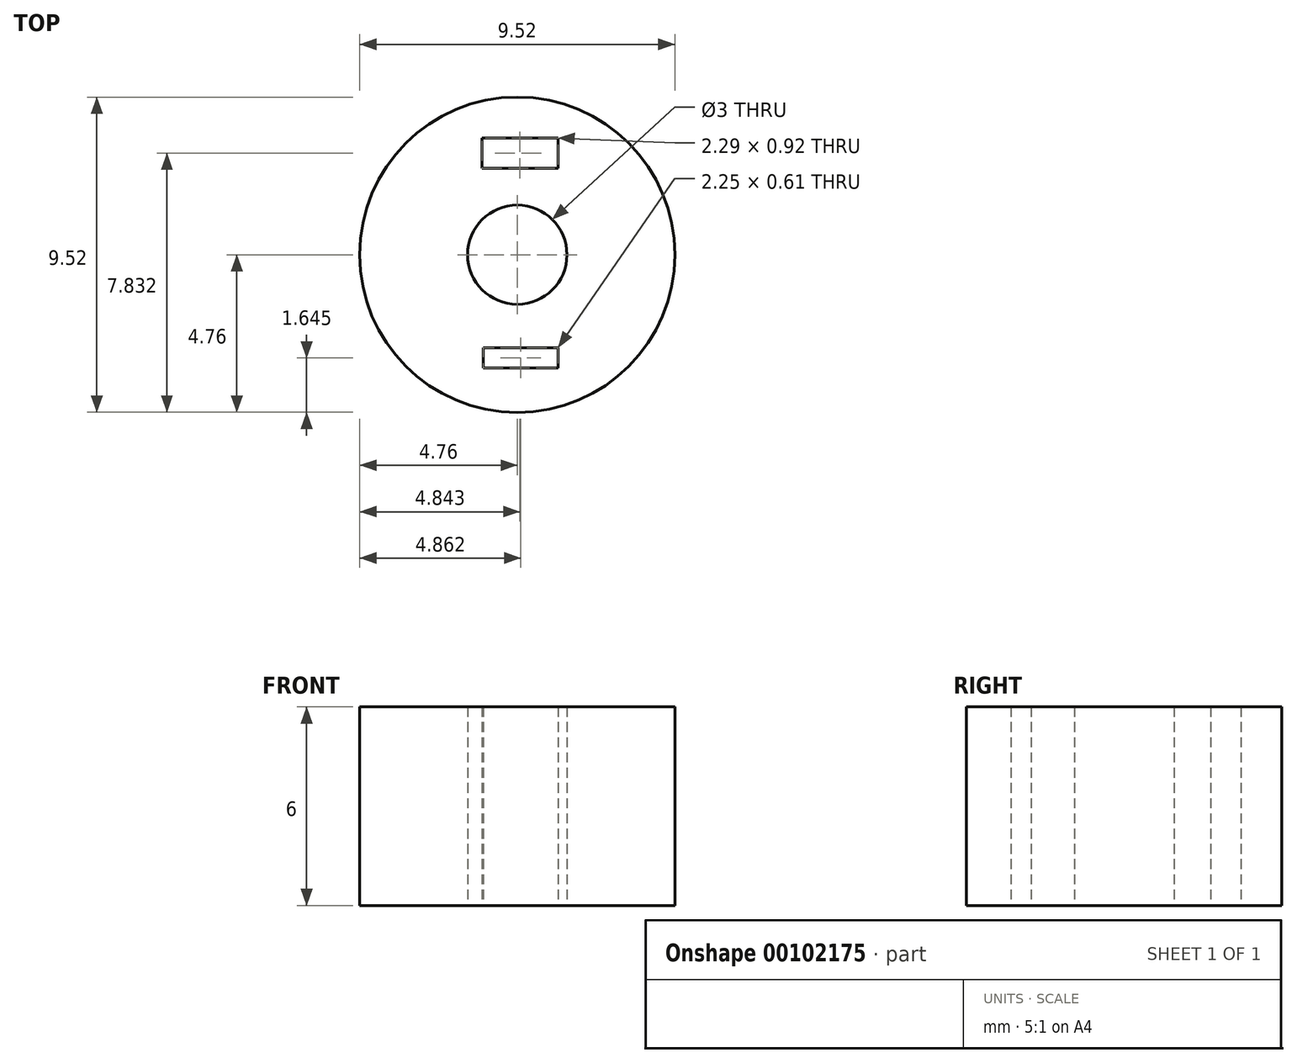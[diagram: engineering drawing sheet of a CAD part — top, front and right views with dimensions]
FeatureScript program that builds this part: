
annotation { "Feature Type Name" : "Feature", "Feature Type Description" : "" }
export const myFeature = defineFeature(function(context is Context, id is Id, definition is map)
    precondition{}
    {
        {
            var Q0;
            Q0=qCreatedBy(makeId("Top.planeOp"),FACE);
            var sketch = newSketch(context, id + "F0", { "sketchPlane" : qUnion([Q0])});
            skCircle(sketch, "E0", {"center": v(0, 0) * mm, "radius": 4.76 * mm});
            skCircle(sketch, "E1", {"center": v(0, 0) * mm, "radius": 1.5 * mm});
            skLineSegment(sketch, "E2.bottom", {"start": v(-1.06, 3.53) * mm, "end": v(1.23, 3.53) * mm});
            skLineSegment(sketch, "E2.top", {"start": v(-1.06, 2.61) * mm, "end": v(1.23, 2.61) * mm});
            skLineSegment(sketch, "E2.left", {"start": v(-1.06, 3.53) * mm, "end": v(-1.06, 2.61) * mm});
            skLineSegment(sketch, "E2.right", {"start": v(1.23, 3.53) * mm, "end": v(1.23, 2.61) * mm});
            skLineSegment(sketch, "E3.bottom", {"start": v(-1.02, -2.8) * mm, "end": v(1.23, -2.8) * mm});
            skLineSegment(sketch, "E3.top", {"start": v(-1.02, -3.42) * mm, "end": v(1.23, -3.42) * mm});
            skLineSegment(sketch, "E3.left", {"start": v(-1.02, -2.8) * mm, "end": v(-1.02, -3.42) * mm});
            skLineSegment(sketch, "E3.right", {"start": v(1.23, -2.8) * mm, "end": v(1.23, -3.42) * mm});
            skSolve(sketch);
        }
        {
            var Q0;
            Q0 = qSketchRegion(id + "F0", true);
            extrude(context, id + "F1", {"entities" : qUnion([Q0]), "depth" : 6 * mm});
        }
    });
